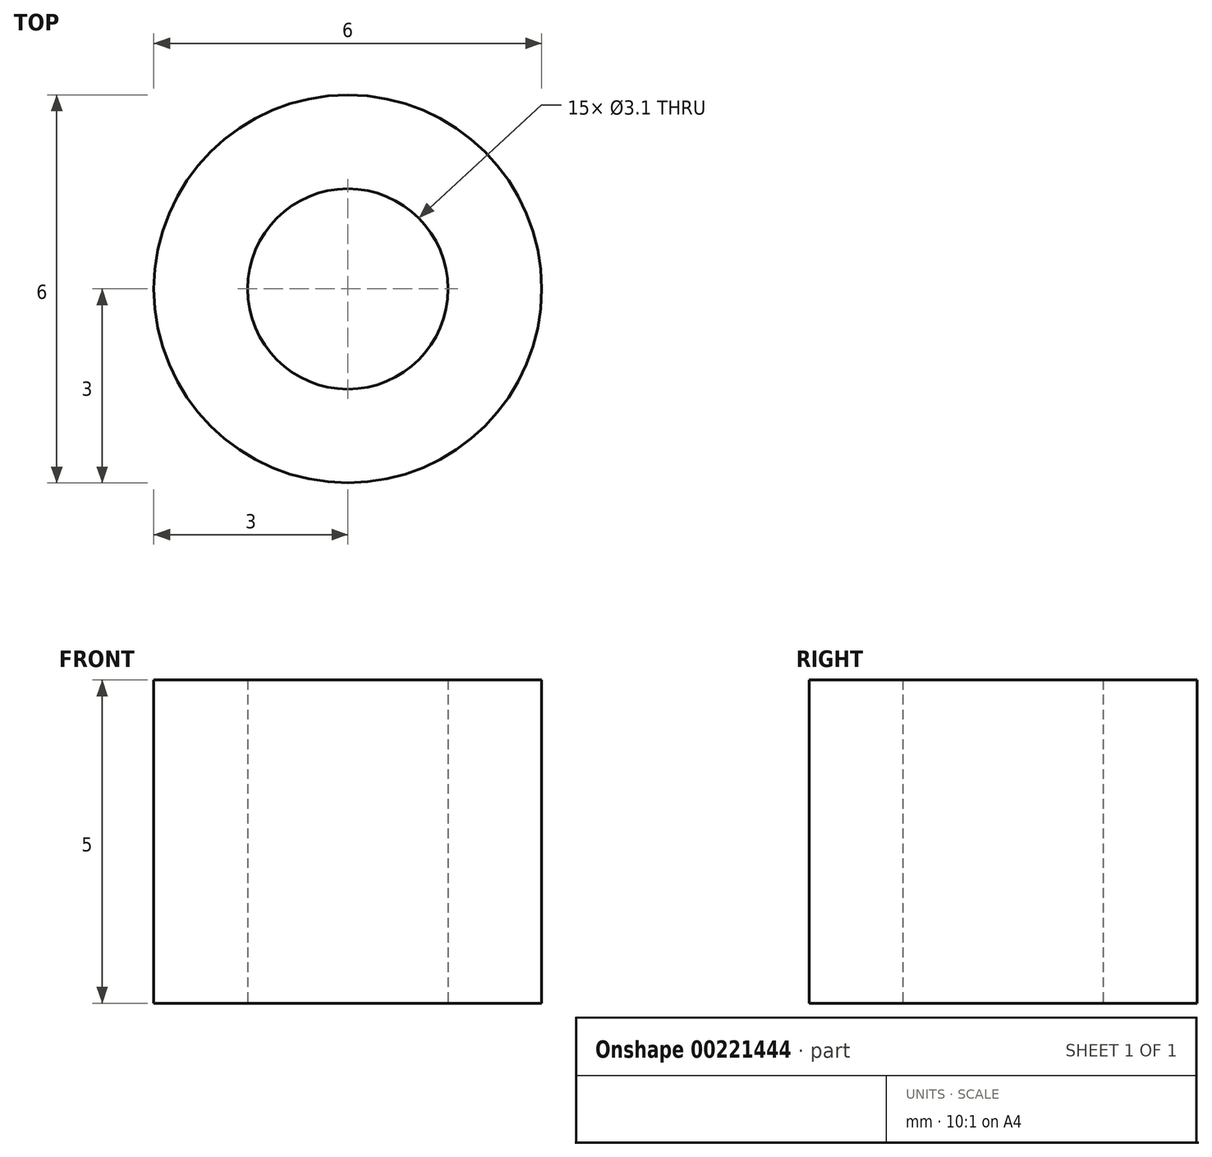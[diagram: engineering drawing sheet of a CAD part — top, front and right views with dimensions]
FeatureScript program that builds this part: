
annotation { "Feature Type Name" : "Feature", "Feature Type Description" : "" }
export const myFeature = defineFeature(function(context is Context, id is Id, definition is map)
    precondition{}
    {
        {
            var Q0;
            Q0=qCreatedBy(makeId("Top.planeOp"),FACE);
            var sketch = newSketch(context, id + "F0", { "sketchPlane" : qUnion([Q0])});
            skCircle(sketch, "E0", {"center": v(0, 0) * mm, "radius": 3 * mm});
            skCircle(sketch, "E1", {"center": v(0, 0) * mm, "radius": 1.55 * mm});
            skSolve(sketch);
        }
        {
            var Q0;
            Q0=makeQuery(id+"F0.imprint","IMPRINT",FACE,{"disambiguationData":[TD([[makeQuery(id+"F0.imprint","IMPRINT",EDGE,{"derivedFrom":sQuery(id+"F0.wireOp",EDGE,"E0")}),1.0]])]});
            extrude(context, id + "F1", {"entities" : qUnion([Q0]), "depth" : 5 * mm});
        }
    });
